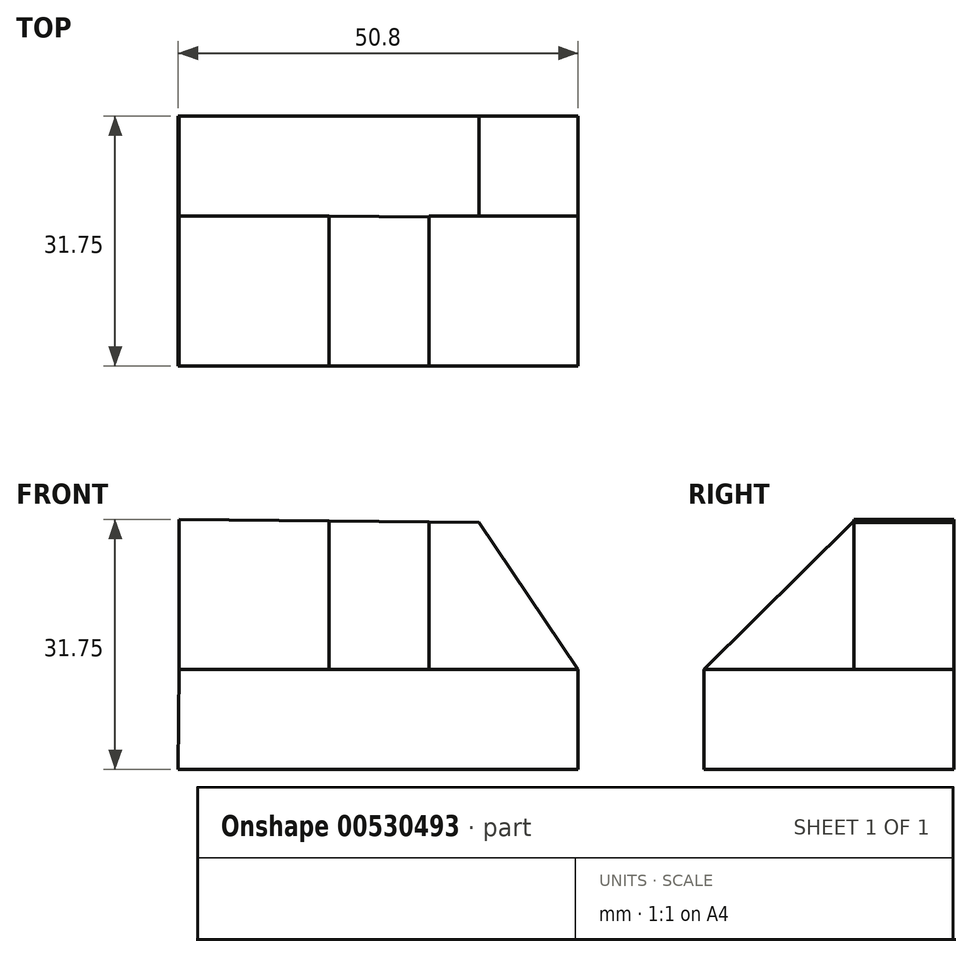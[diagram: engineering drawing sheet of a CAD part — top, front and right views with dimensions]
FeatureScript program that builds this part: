
annotation { "Feature Type Name" : "Feature", "Feature Type Description" : "" }
export const myFeature = defineFeature(function(context is Context, id is Id, definition is map)
    precondition{}
    {
        {
            var Q0;
            Q0=qCreatedBy(makeId("Front.planeOp"),FACE);
            var sketch = newSketch(context, id + "F0", { "sketchPlane" : qUnion([Q0])});
            skLineSegment(sketch, "E0", {"start": v(-59.52, 0) * mm, "end": v(-8.72, 0) * mm});
            skLineSegment(sketch, "E1", {"start": v(-8.72, 0) * mm, "end": v(-8.72, 12.7) * mm});
            skLineSegment(sketch, "E2", {"start": v(-8.72, 12.7) * mm, "end": v(-59.39, 12.7) * mm});
            skLineSegment(sketch, "E3", {"start": v(-59.39, 12.7) * mm, "end": v(-59.52, 0) * mm});
            skLineSegment(sketch, "E4", {"start": v(-59.39, 12.7) * mm, "end": v(-59.39, 31.75) * mm});
            skLineSegment(sketch, "E5", {"start": v(-59.39, 31.75) * mm, "end": v(-21.29, 31.35) * mm});
            skLineSegment(sketch, "E6", {"start": v(-21.29, 31.35) * mm, "end": v(-8.72, 12.7) * mm});
            skSolve(sketch);
        }
        {
            var Q0;
            Q0 = qSketchRegion(id + "F0", true);
            extrude(context, id + "F1", {"entities" : qUnion([Q0]), "depth" : 31.75 * mm, "offsetDistance" : 25.4 * mm});
        }
        {
            var Q0;
            Q0=makeQuery(id+"F1.opExtrude","SWEPT_FACE",FACE,{"disambiguationData":[OSD([sQuery(id+"F0.wireOp",EDGE,"E4")])]});
            var sketch = newSketch(context, id + "F2", { "sketchPlane" : qUnion([Q0])});
            skLineSegment(sketch, "E7", {"start": v(12.7, 31.75) * mm, "end": v(12.7, 12.7) * mm});
            skLineSegment(sketch, "E8", {"start": v(12.7, 12.7) * mm, "end": v(31.75, 12.7) * mm});
            skLineSegment(sketch, "E9", {"start": v(31.75, 12.7) * mm, "end": v(31.75, 31.75) * mm});
            skLineSegment(sketch, "E10", {"start": v(31.75, 31.75) * mm, "end": v(12.7, 31.75) * mm});
            skSolve(sketch);
        }
        {
            var Q0;
            Q0=makeQuery(id+"F2.imprint","IMPRINT",FACE,{"disambiguationData":[TD([[makeQuery(id+"F2.imprint","IMPRINT",EDGE,{"derivedFrom":sQuery(id+"F2.wireOp",EDGE,"E7")}),1.0]])]});
            extrude(context, id + "F3", {"entities" : qUnion([Q0]), "operationType" : NewBodyOperationType.REMOVE, "oppositeDirection" : true, "depth" : 19.05 * mm, "offsetDistance" : 25.4 * mm});
        }
        {
            var Q0;
            Q0=makeQuery(id+"F3.boolean.opBoolean","COPY",FACE,{"derivedFrom":makeQuery(id+"F3.opExtrude","CAP_FACE",FACE,{"disambiguationData":[OSD([sQuery(id+"F2.wireOp",EDGE,"E7"),sQuery(id+"F2.wireOp",EDGE,"E8"),sQuery(id+"F2.wireOp",EDGE,"E9"),sQuery(id+"F2.wireOp",EDGE,"E10")])],"isStart":false})});
            var sketch = newSketch(context, id + "F4", { "sketchPlane" : qUnion([Q0])});
            skLineSegment(sketch, "E11", {"start": v(31.75, 12.7) * mm, "end": v(12.7, 31.55) * mm});
            skLineSegment(sketch, "E12", {"start": v(12.7, 31.55) * mm, "end": v(31.75, 31.55) * mm});
            skLineSegment(sketch, "E13", {"start": v(31.75, 31.55) * mm, "end": v(31.75, 12.7) * mm});
            skSolve(sketch);
        }
        {
            var Q0;
            Q0=makeQuery(id+"F4.imprint","IMPRINT",FACE,{"disambiguationData":[TD([[makeQuery(id+"F4.imprint","IMPRINT",EDGE,{"derivedFrom":sQuery(id+"F4.wireOp",EDGE,"E11")}),-1.0]])]});
            extrude(context, id + "F5", {"entities" : qUnion([Q0]), "operationType" : NewBodyOperationType.REMOVE, "oppositeDirection" : true, "depth" : 12.7 * mm, "offsetDistance" : 25.4 * mm});
        }
        {
            var Q0;
            Q0=makeQuery(id+"F1.opExtrude","CAP_FACE",FACE,{"disambiguationData":[OSD([sQuery(id+"F0.wireOp",EDGE,"E0"),sQuery(id+"F0.wireOp",EDGE,"E1"),sQuery(id+"F0.wireOp",EDGE,"E3"),sQuery(id+"F0.wireOp",EDGE,"E4"),sQuery(id+"F0.wireOp",EDGE,"E5"),sQuery(id+"F0.wireOp",EDGE,"E6")])],"isStart":false});
            var sketch = newSketch(context, id + "F6", { "sketchPlane" : qUnion([Q0])});
            skLineSegment(sketch, "E14", {"start": v(-27.64, 12.7) * mm, "end": v(-8.72, 12.7) * mm});
            skLineSegment(sketch, "E15", {"start": v(-8.72, 12.7) * mm, "end": v(-21.29, 31.35) * mm});
            skLineSegment(sketch, "E16", {"start": v(-21.29, 31.35) * mm, "end": v(-27.64, 31.42) * mm});
            skLineSegment(sketch, "E17", {"start": v(-27.64, 31.42) * mm, "end": v(-27.64, 12.7) * mm});
            skSolve(sketch);
        }
        {
            var Q0;
            Q0=makeQuery(id+"F6.imprint","IMPRINT",FACE,{"disambiguationData":[TD([[makeQuery(id+"F6.imprint","IMPRINT",EDGE,{"derivedFrom":sQuery(id+"F6.wireOp",EDGE,"E14")}),1.0]])]});
            extrude(context, id + "F7", {"entities" : qUnion([Q0]), "operationType" : NewBodyOperationType.REMOVE, "oppositeDirection" : true, "depth" : 19.05 * mm, "offsetDistance" : 25.4 * mm});
        }
    });
